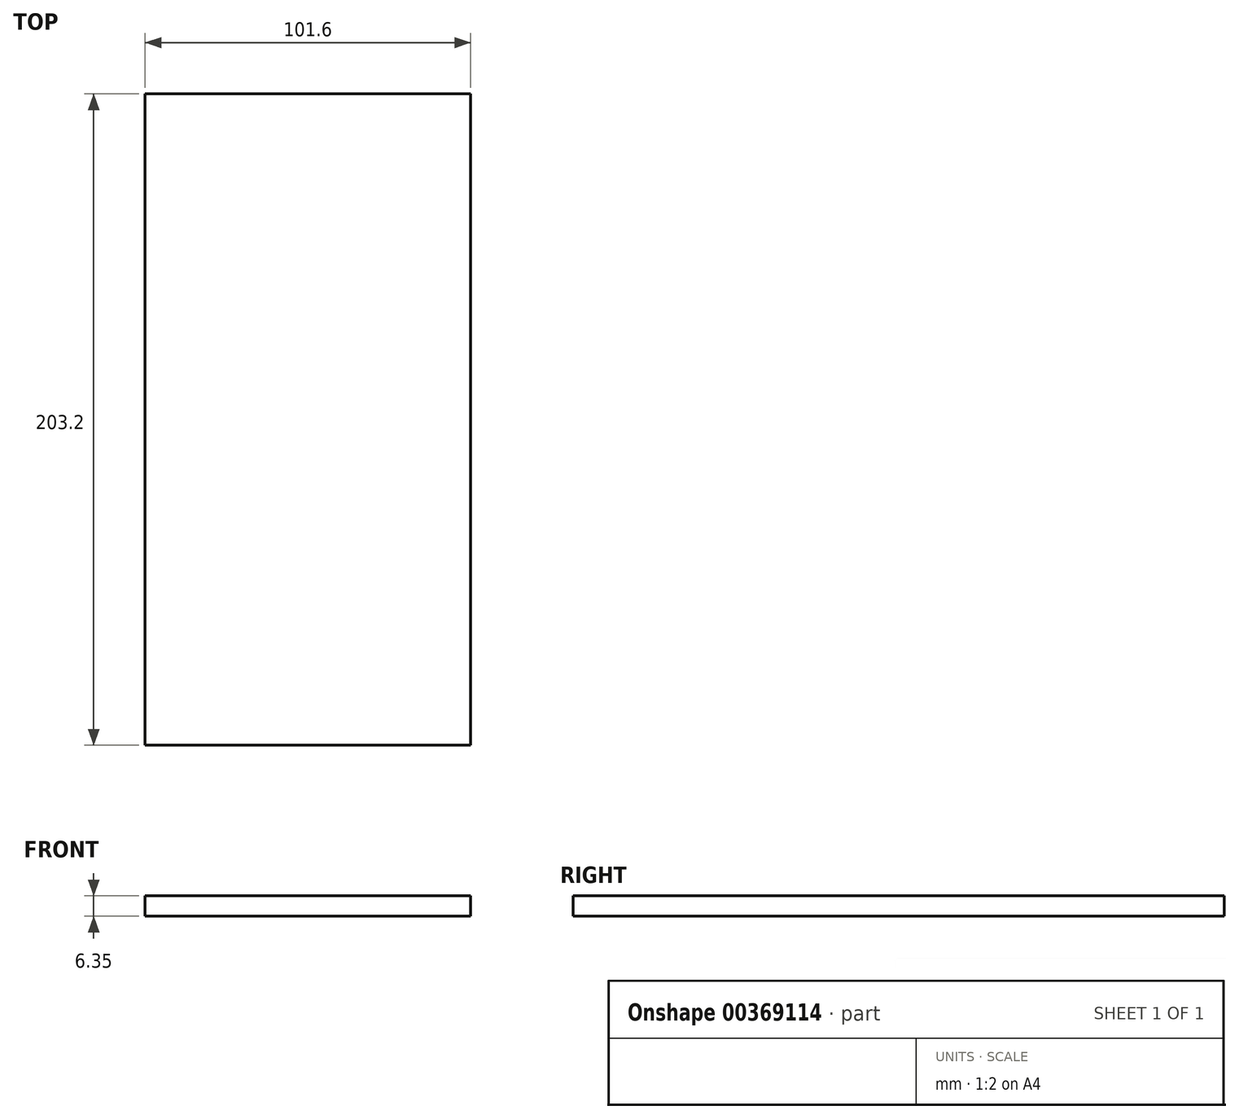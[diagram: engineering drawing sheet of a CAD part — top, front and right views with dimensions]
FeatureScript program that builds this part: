
annotation { "Feature Type Name" : "Feature", "Feature Type Description" : "" }
export const myFeature = defineFeature(function(context is Context, id is Id, definition is map)
    precondition{}
    {
        {
            var Q0;
            Q0=qCreatedBy(makeId("Top.planeOp"),FACE);
            var sketch = newSketch(context, id + "F0", { "sketchPlane" : qUnion([Q0])});
            skLineSegment(sketch, "E0.bottom", {"start": v(0, 0) * mm, "end": v(101.6, 0) * mm});
            skLineSegment(sketch, "E0.top", {"start": v(0, -203.2) * mm, "end": v(101.6, -203.2) * mm});
            skLineSegment(sketch, "E0.left", {"start": v(0, 0) * mm, "end": v(0, -203.2) * mm});
            skLineSegment(sketch, "E0.right", {"start": v(101.6, 0) * mm, "end": v(101.6, -203.2) * mm});
            skSolve(sketch);
        }
        {
            var Q0;
            Q0=makeQuery(id+"F0.imprint","IMPRINT",FACE,{"disambiguationData":[TD([[makeQuery(id+"F0.imprint","IMPRINT",EDGE,{"derivedFrom":sQuery(id+"F0.wireOp",EDGE,"E0.bottom")}),-1.0]])]});
            extrude(context, id + "F1", {"entities" : qUnion([Q0]), "depth" : 6.35 * mm});
        }
    });
